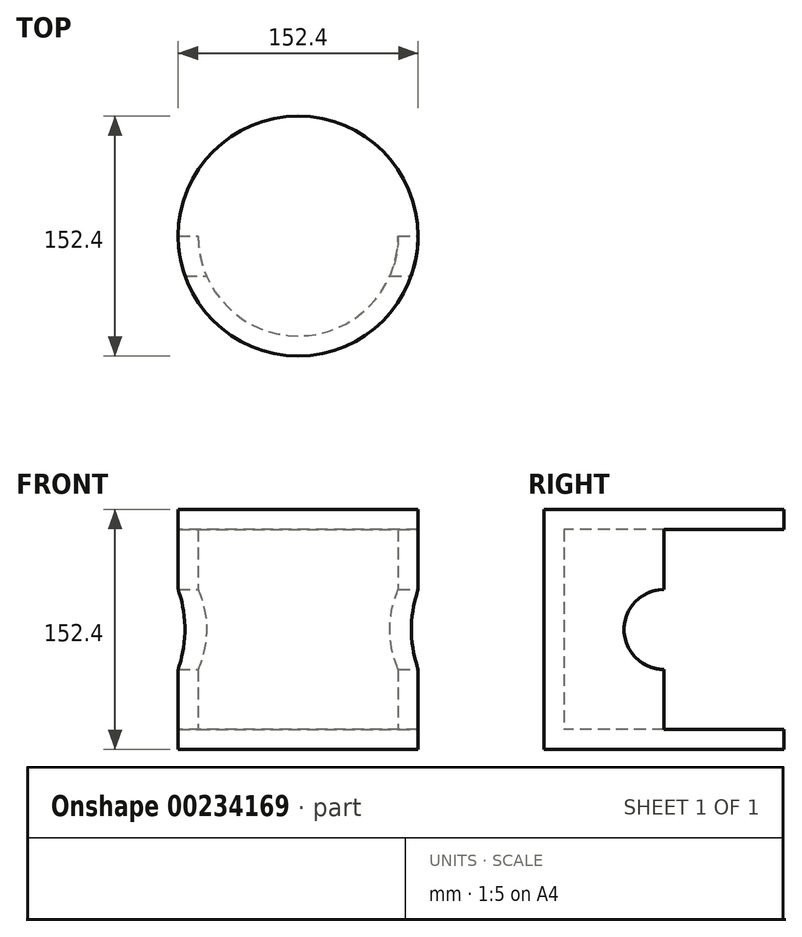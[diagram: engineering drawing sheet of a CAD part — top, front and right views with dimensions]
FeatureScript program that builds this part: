
annotation { "Feature Type Name" : "Feature", "Feature Type Description" : "" }
export const myFeature = defineFeature(function(context is Context, id is Id, definition is map)
    precondition{}
    {
        {
            var Q0;
            Q0=qCreatedBy(makeId("Top.planeOp"),FACE);
            var sketch = newSketch(context, id + "F0", { "sketchPlane" : qUnion([Q0])});
            skCircle(sketch, "E0", {"center": v(0, 0) * mm, "radius": 76.2 * mm});
            skSolve(sketch);
        }
        {
            var Q0;
            Q0 = qSketchRegion(id + "F0", true);
            extrude(context, id + "F1", {"entities" : qUnion([Q0]), "depth" : 152.4 * mm});
        }
        {
            var Q0;
            Q0=qCreatedBy(makeId("Right.planeOp"),FACE);
            var sketch = newSketch(context, id + "F2", { "sketchPlane" : qUnion([Q0])});
            skLineSegment(sketch, "E1.bottom", {"start": v(76.77, 139.7) * mm, "end": v(0, 139.7) * mm});
            skLineSegment(sketch, "E1.top", {"start": v(76.77, 12.7) * mm, "end": v(0, 12.7) * mm});
            skLineSegment(sketch, "E1.left", {"start": v(76.77, 139.7) * mm, "end": v(76.77, 12.7) * mm});
            skLineSegment(sketch, "E1.right", {"start": v(0, 139.7) * mm, "end": v(0, 12.7) * mm});
            skSolve(sketch);
        }
        {
            var Q0;
            Q0 = qSketchRegion(id + "F2", true);
            extrude(context, id + "F3", {"entities" : qUnion([Q0]), "operationType" : NewBodyOperationType.REMOVE, "endBound" : BoundingType.SYMMETRIC, "oppositeDirection" : true, "depth" : 152.4 * mm});
        }
        {
            var Q0;
            Q0=makeQuery(id+"F3.boolean.opBoolean","COPY",FACE,{"derivedFrom":makeQuery(id+"F3.opExtrude","SWEPT_FACE",FACE,{"disambiguationData":[OSD([sQuery(id+"F2.wireOp",EDGE,"E1.top")])]})});
            var sketch = newSketch(context, id + "F4", { "sketchPlane" : qUnion([Q0])});
            skCircle(sketch, "E2", {"center": v(0, 0) * mm, "radius": 63.5 * mm});
            skSolve(sketch);
        }
        {
            var Q0;
            Q0 = qSketchRegion(id + "F4", true);
            extrude(context, id + "F5", {"entities" : qUnion([Q0]), "operationType" : NewBodyOperationType.REMOVE, "depth" : 127 * mm});
        }
        {
            var Q0;
            Q0=qCreatedBy(makeId("Right.planeOp"),FACE);
            var sketch = newSketch(context, id + "F6", { "sketchPlane" : qUnion([Q0])});
            skCircle(sketch, "E3", {"center": v(0, 76.2) * mm, "radius": 25.4 * mm});
            skSolve(sketch);
        }
        {
            var Q0;
            Q0=makeQuery(id+"F6.imprint","IMPRINT",FACE,{"disambiguationData":[TD([[makeQuery(id+"F6.imprint","IMPRINT",EDGE,{"derivedFrom":sQuery(id+"F6.wireOp",EDGE,"E3")}),1.0]])]});
            extrude(context, id + "F7", {"entities" : qUnion([Q0]), "operationType" : NewBodyOperationType.REMOVE, "endBound" : BoundingType.SYMMETRIC, "oppositeDirection" : true, "depth" : 152.4 * mm});
        }
    });
